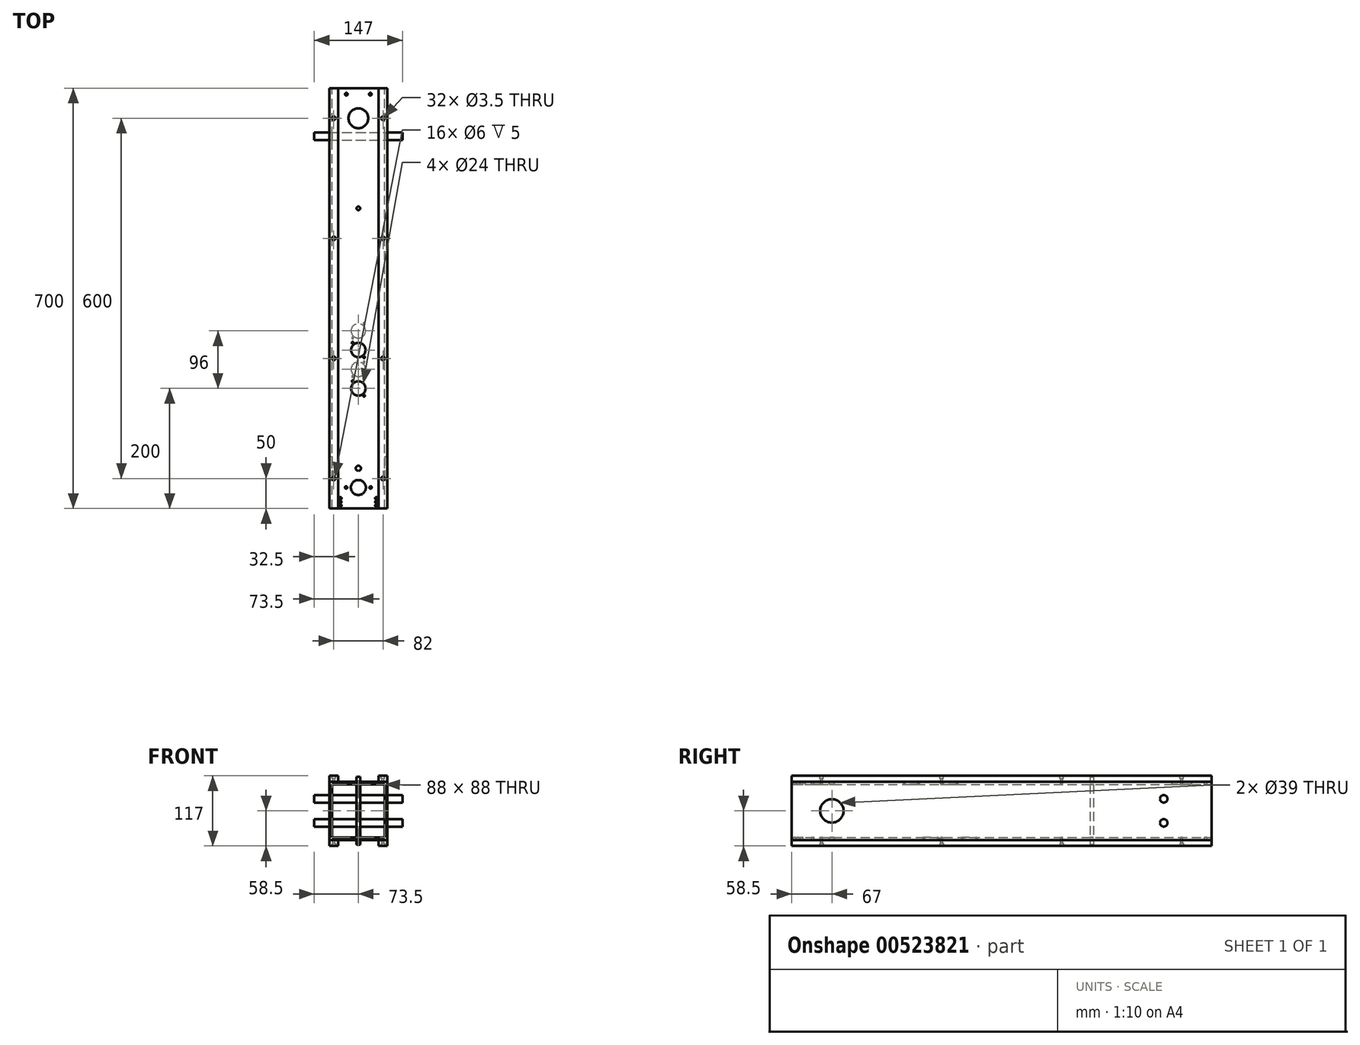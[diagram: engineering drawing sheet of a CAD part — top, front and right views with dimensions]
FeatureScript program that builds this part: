
annotation { "Feature Type Name" : "Feature", "Feature Type Description" : "" }
export const myFeature = defineFeature(function(context is Context, id is Id, definition is map)
    precondition{}
    {
        {
            var Q0;
            Q0=qCreatedBy(makeId("Front.planeOp"),FACE);
            var sketch = newSketch(context, id + "F0", { "sketchPlane" : qUnion([Q0])});
            skLineSegment(sketch, "E0.bottom", {"start": v(0, 0) * mm, "end": v(97, 0) * mm});
            skLineSegment(sketch, "E0.top", {"start": v(0, 97) * mm, "end": v(97, 97) * mm});
            skLineSegment(sketch, "E0.left", {"start": v(0, 0) * mm, "end": v(0, 97) * mm});
            skLineSegment(sketch, "E0.right", {"start": v(97, 0) * mm, "end": v(97, 97) * mm});
            skLineSegment(sketch, "E1.bottom", {"start": v(4.5, 92.5) * mm, "end": v(92.5, 92.5) * mm});
            skLineSegment(sketch, "E1.top", {"start": v(4.5, 4.5) * mm, "end": v(92.5, 4.5) * mm});
            skLineSegment(sketch, "E1.left", {"start": v(4.5, 92.5) * mm, "end": v(4.5, 4.5) * mm});
            skLineSegment(sketch, "E1.right", {"start": v(92.5, 92.5) * mm, "end": v(92.5, 4.5) * mm});
            skSolve(sketch);
        }
        {
            var Q0;
            Q0=makeQuery(id+"F0.imprint","IMPRINT",FACE,{"disambiguationData":[TD([[makeQuery(id+"F0.imprint","IMPRINT",EDGE,{"derivedFrom":sQuery(id+"F0.wireOp",EDGE,"E0.bottom")}),1.0]])]});
            extrude(context, id + "F1", {"entities" : qUnion([Q0]), "depth" : 700 * mm, "offsetDistance" : 25 * mm});
        }
        {
            var Q0;
            Q0=makeQuery(id+"F1.opExtrude","SWEPT_FACE",FACE,{"disambiguationData":[OSD([sQuery(id+"F0.wireOp",EDGE,"E0.top")])]});
            var sketch = newSketch(context, id + "F2", { "sketchPlane" : qUnion([Q0])});
            skLineSegment(sketch, "E2.bottom", {"start": v(0, 0) * mm, "end": v(15, 0) * mm});
            skLineSegment(sketch, "E2.top", {"start": v(0, -700) * mm, "end": v(15, -700) * mm});
            skLineSegment(sketch, "E2.left", {"start": v(0, 0) * mm, "end": v(0, -700) * mm});
            skLineSegment(sketch, "E2.right", {"start": v(15, 0) * mm, "end": v(15, -700) * mm});
            skLineSegment(sketch, "E3.bottom", {"start": v(97, 0) * mm, "end": v(82, 0) * mm});
            skLineSegment(sketch, "E3.top", {"start": v(97, -700) * mm, "end": v(82, -700) * mm});
            skLineSegment(sketch, "E3.left", {"start": v(97, 0) * mm, "end": v(97, -700) * mm});
            skLineSegment(sketch, "E3.right", {"start": v(82, 0) * mm, "end": v(82, -700) * mm});
            skSolve(sketch);
        }
        {
            var Q0;
            Q0 = qSketchRegion(id + "F2", true);
            extrude(context, id + "F3", {"entities" : qUnion([Q0]), "depth" : 10 * mm, "offsetDistance" : 25 * mm});
        }
        {
            var Q0;
            Q0=makeQuery(id+"F1.opExtrude","SWEPT_FACE",FACE,{"disambiguationData":[OSD([sQuery(id+"F0.wireOp",EDGE,"E0.bottom")])]});
            var sketch = newSketch(context, id + "F4", { "sketchPlane" : qUnion([Q0])});
            skLineSegment(sketch, "E4.bottom", {"start": v(0, 700) * mm, "end": v(15, 700) * mm});
            skLineSegment(sketch, "E4.top", {"start": v(0, 0) * mm, "end": v(15, 0) * mm});
            skLineSegment(sketch, "E4.left", {"start": v(0, 700) * mm, "end": v(0, 0) * mm});
            skLineSegment(sketch, "E4.right", {"start": v(15, 700) * mm, "end": v(15, 0) * mm});
            skLineSegment(sketch, "E5.bottom", {"start": v(97, 700) * mm, "end": v(82, 700) * mm});
            skLineSegment(sketch, "E5.top", {"start": v(97, 0) * mm, "end": v(82, 0) * mm});
            skLineSegment(sketch, "E5.left", {"start": v(97, 700) * mm, "end": v(97, 0) * mm});
            skLineSegment(sketch, "E5.right", {"start": v(82, 700) * mm, "end": v(82, 0) * mm});
            skSolve(sketch);
        }
        {
            var Q0;
            Q0 = qSketchRegion(id + "F4", true);
            extrude(context, id + "F5", {"entities" : qUnion([Q0]), "depth" : 10 * mm, "offsetDistance" : 25 * mm});
        }
        {
            var Q0;
            {var subQ0=sQuery(id+"F2.wireOp",EDGE,"E2.right");Q0=makeQuery(id+"F2.imprint","IMPRINT",FACE,{"disambiguationData":[TD([[makeQuery(id+"F2.imprint","IMPRINT",EDGE,{"derivedFrom":subQ0}),1.0]])]});}
            var sketch = newSketch(context, id + "F6", { "sketchPlane" : qUnion([Q0])});
            skLineSegment(sketch, "E6", {"start": v(48.5, -700) * mm, "end": v(48.5, 0) * mm, "construction": true});
            skCircle(sketch, "E7", {"center": v(48.5, -633) * mm, "radius": 4.25 * mm});
            skCircle(sketch, "E8", {"center": v(48.5, -665) * mm, "radius": 12.5 * mm});
            skCircle(sketch, "E9", {"center": v(28, -665) * mm, "radius": 2 * mm});
            skCircle(sketch, "E10", {"center": v(69, -665) * mm, "radius": 2 * mm});
            skLineSegment(sketch, "E11", {"start": v(28, -665) * mm, "end": v(69, -665) * mm, "construction": true});
            skCircle(sketch, "E12", {"center": v(48.5, -500) * mm, "radius": 12 * mm});
            skCircle(sketch, "E13", {"center": v(39, -488) * mm, "radius": 1.5 * mm});
            skCircle(sketch, "E14", {"center": v(58, -512) * mm, "radius": 1.5 * mm});
            skLineSegment(sketch, "E15", {"start": v(58, -512) * mm, "end": v(39, -488) * mm, "construction": true});
            skCircle(sketch, "E16.0.1.0", {"center": v(48.5, -436) * mm, "radius": 12 * mm});
            skCircle(sketch, "E16.0.1.1", {"center": v(39, -424) * mm, "radius": 1.5 * mm});
            skCircle(sketch, "E16.0.1.2", {"center": v(58, -448) * mm, "radius": 1.5 * mm});
            skLineSegment(sketch, "E16.direction1", {"start": v(48.5, -500) * mm, "end": v(74.81, -500) * mm, "construction": true});
            skLineSegment(sketch, "E16.direction2", {"start": v(48.5, -500) * mm, "end": v(48.5, -436) * mm, "construction": true});
            skArc(sketch, "E17", {"start": v(20.5, -683) * mm, "mid": v(18.5, -681) * mm, "end": v(16.5, -683) * mm});
            skArc(sketch, "E18", {"start": v(80.5, -683) * mm, "mid": v(78.5, -681) * mm, "end": v(76.5, -683) * mm});
            skLineSegment(sketch, "E19", {"start": v(48.5, -683) * mm, "end": v(78.5, -683) * mm, "construction": true});
            skLineSegment(sketch, "E20", {"start": v(48.5, -683) * mm, "end": v(18.5, -683) * mm, "construction": true});
            skCircle(sketch, "E21", {"center": v(48.5, -633) * mm, "radius": 19.5 * mm, "construction": true});
            skCircle(sketch, "E22", {"center": v(48.5, -665) * mm, "radius": 8.5 * mm, "construction": true});
            skArc(sketch, "E23", {"start": v(16.5, -695) * mm, "mid": v(18.5, -697) * mm, "end": v(20.5, -695) * mm});
            skArc(sketch, "E24", {"start": v(76.5, -695) * mm, "mid": v(78.5, -697) * mm, "end": v(80.5, -695) * mm});
            skCircle(sketch, "E25", {"center": v(28.5, -10) * mm, "radius": 2.25 * mm});
            skCircle(sketch, "E26", {"center": v(68.5, -10) * mm, "radius": 2.25 * mm});
            skLineSegment(sketch, "E27", {"start": v(28.5, -10) * mm, "end": v(48.5, -10) * mm, "construction": true});
            skLineSegment(sketch, "E28", {"start": v(48.5, -10) * mm, "end": v(68.5, -10) * mm, "construction": true});
            skCircle(sketch, "E29", {"center": v(48.5, -50) * mm, "radius": 16.5 * mm});
            skCircle(sketch, "E30", {"center": v(48.5, -665) * mm, "radius": 6 * mm, "construction": true});
            skCircle(sketch, "E31", {"center": v(48.5, -200) * mm, "radius": 3 * mm});
            skCircle(sketch, "E32", {"center": v(18.5, -683) * mm, "radius": 2 * mm});
            skCircle(sketch, "E33", {"center": v(18.5, -695) * mm, "radius": 2 * mm});
            skLineSegment(sketch, "E34", {"start": v(18.5, -683) * mm, "end": v(18.5, -695) * mm, "construction": true});
            skCircle(sketch, "E35", {"center": v(18.5, -689) * mm, "radius": 2 * mm});
            skCircle(sketch, "E36", {"center": v(78.5, -683) * mm, "radius": 2 * mm});
            skCircle(sketch, "E37", {"center": v(78.5, -695) * mm, "radius": 2 * mm});
            skLineSegment(sketch, "E38", {"start": v(78.5, -683) * mm, "end": v(78.5, -695) * mm, "construction": true});
            skCircle(sketch, "E39", {"center": v(78.5, -689) * mm, "radius": 2 * mm});
            skSolve(sketch);
        }
        {
            var Q0;
            Q0=makeQuery(id+"F6.imprint","IMPRINT",FACE,{"disambiguationData":[TD([[makeQuery(id+"F6.imprint","IMPRINT",EDGE,{"derivedFrom":sQuery(id+"F6.wireOp",EDGE,"E8")}),1.0]])]});
            var Q1;
            Q1=makeQuery(id+"F6.imprint","IMPRINT",FACE,{"disambiguationData":[TD([[makeQuery(id+"F6.imprint","IMPRINT",EDGE,{"derivedFrom":sQuery(id+"F6.wireOp",EDGE,"E12")}),1.0]])]});
            var Q2;
            Q2=makeQuery(id+"F6.imprint","IMPRINT",FACE,{"disambiguationData":[TD([[makeQuery(id+"F6.imprint","IMPRINT",EDGE,{"derivedFrom":sQuery(id+"F6.wireOp",EDGE,"E16.0.1.0")}),1.0]])]});
            var Q3;
            Q3=makeQuery(id+"F6.imprint","IMPRINT",FACE,{"disambiguationData":[TD([[makeQuery(id+"F6.imprint","IMPRINT",EDGE,{"derivedFrom":sQuery(id+"F6.wireOp",EDGE,"E16.0.1.2")}),1.0]])]});
            var Q4;
            Q4=makeQuery(id+"F6.imprint","IMPRINT",FACE,{"disambiguationData":[TD([[makeQuery(id+"F6.imprint","IMPRINT",EDGE,{"derivedFrom":sQuery(id+"F6.wireOp",EDGE,"E16.0.1.1")}),1.0]])]});
            var Q5;
            Q5=makeQuery(id+"F6.imprint","IMPRINT",FACE,{"disambiguationData":[TD([[makeQuery(id+"F6.imprint","IMPRINT",EDGE,{"derivedFrom":sQuery(id+"F6.wireOp",EDGE,"E13")}),1.0]])]});
            var Q6;
            Q6=makeQuery(id+"F6.imprint","IMPRINT",FACE,{"disambiguationData":[TD([[makeQuery(id+"F6.imprint","IMPRINT",EDGE,{"derivedFrom":sQuery(id+"F6.wireOp",EDGE,"E14")}),1.0]])]});
            extrude(context, id + "F7", {"entities" : qUnion([Q0, Q1, Q2, Q3, Q4, Q5, Q6]), "operationType" : NewBodyOperationType.REMOVE, "oppositeDirection" : true, "depth" : 25 * mm, "offsetDistance" : 25 * mm});
        }
        {
            var Q0;
            Q0=makeQuery(id+"F6.imprint","IMPRINT",FACE,{"disambiguationData":[TD([[makeQuery(id+"F6.imprint","IMPRINT",EDGE,{"derivedFrom":sQuery(id+"F6.wireOp",EDGE,"E7")}),1.0]])]});
            var Q1;
            Q1=makeQuery(id+"F6.imprint","IMPRINT",FACE,{"disambiguationData":[TD([[makeQuery(id+"F6.imprint","IMPRINT",EDGE,{"derivedFrom":sQuery(id+"F6.wireOp",EDGE,"E10")}),1.0]])]});
            var Q2;
            Q2=makeQuery(id+"F6.imprint","IMPRINT",FACE,{"disambiguationData":[TD([[makeQuery(id+"F6.imprint","IMPRINT",EDGE,{"derivedFrom":sQuery(id+"F6.wireOp",EDGE,"E9")}),1.0]])]});
            extrude(context, id + "F8", {"entities" : qUnion([Q0, Q1, Q2]), "operationType" : NewBodyOperationType.REMOVE, "oppositeDirection" : true, "depth" : 150 * mm, "offsetDistance" : 25 * mm});
        }
        {
            var Q0;
            Q0=makeQuery(id+"F1.opExtrude","SWEPT_FACE",FACE,{"disambiguationData":[OSD([sQuery(id+"F0.wireOp",EDGE,"E0.bottom")])]});
            var sketch = newSketch(context, id + "F9", { "sketchPlane" : qUnion([Q0])});
            skLineSegment(sketch, "E40", {"start": v(48.5, 700) * mm, "end": v(48.5, 0) * mm, "construction": true});
            skCircle(sketch, "E41", {"center": v(48.5, 468) * mm, "radius": 12 * mm});
            skCircle(sketch, "E42", {"center": v(39, 480) * mm, "radius": 1.5 * mm});
            skCircle(sketch, "E43", {"center": v(58, 456) * mm, "radius": 1.5 * mm});
            skLineSegment(sketch, "E44", {"start": v(58, 456) * mm, "end": v(39, 480) * mm, "construction": true});
            skCircle(sketch, "E45.0.1.0", {"center": v(48.5, 404) * mm, "radius": 12 * mm});
            skCircle(sketch, "E45.0.1.1", {"center": v(58, 392) * mm, "radius": 1.5 * mm});
            skCircle(sketch, "E45.0.1.2", {"center": v(39, 416) * mm, "radius": 1.5 * mm});
            skLineSegment(sketch, "E45.direction1", {"start": v(48.5, 468) * mm, "end": v(75, 468) * mm, "construction": true});
            skLineSegment(sketch, "E45.direction2", {"start": v(48.5, 468) * mm, "end": v(48.5, 404) * mm, "construction": true});
            skSolve(sketch);
        }
        {
            var Q0;
            Q0 = qSketchRegion(id + "F9", true);
            extrude(context, id + "F10", {"entities" : qUnion([Q0]), "operationType" : NewBodyOperationType.REMOVE, "oppositeDirection" : true, "depth" : 25 * mm, "offsetDistance" : 25 * mm});
        }
        {
            var Q0;
            Q0=makeQuery(id+"F1.opExtrude","SWEPT_FACE",FACE,{"disambiguationData":[OSD([sQuery(id+"F0.wireOp",EDGE,"E0.right")])]});
            var sketch = newSketch(context, id + "F11", { "sketchPlane" : qUnion([Q0])});
            skLineSegment(sketch, "E46", {"start": v(-700, 48.5) * mm, "end": v(0, 48.5) * mm, "construction": true});
            skCircle(sketch, "E47", {"center": v(-633, 48.5) * mm, "radius": 19.5 * mm});
            skCircle(sketch, "E48", {"center": v(-80, 68.5) * mm, "radius": 6.26 * mm});
            skCircle(sketch, "E49", {"center": v(-80, 28.5) * mm, "radius": 6.26 * mm});
            skLineSegment(sketch, "E50", {"start": v(-80, 68.5) * mm, "end": v(-80, 48.5) * mm, "construction": true});
            skLineSegment(sketch, "E51", {"start": v(-80, 48.5) * mm, "end": v(-80, 28.5) * mm, "construction": true});
            skSolve(sketch);
        }
        {
            var Q0;
            Q0 = qSketchRegion(id + "F11", true);
            extrude(context, id + "F12", {"entities" : qUnion([Q0]), "operationType" : NewBodyOperationType.REMOVE, "oppositeDirection" : true, "depth" : 150 * mm, "offsetDistance" : 25 * mm});
        }
        {
            var Q0;
            Q0=makeQuery(id+"F6.imprint","IMPRINT",FACE,{"disambiguationData":[TD([[makeQuery(id+"F6.imprint","IMPRINT",EDGE,{"derivedFrom":sQuery(id+"F6.wireOp",EDGE,"E17")}),1.0]])]});
            var Q1;
            Q1=makeQuery(id+"F6.imprint","IMPRINT",FACE,{"disambiguationData":[TD([[makeQuery(id+"F6.imprint","IMPRINT",EDGE,{"derivedFrom":sQuery(id+"F6.wireOp",EDGE,"E18")}),1.0]])]});
            extrude(context, id + "F13", {"entities" : qUnion([Q0, Q1]), "operationType" : NewBodyOperationType.REMOVE, "oppositeDirection" : true, "depth" : 150 * mm, "offsetDistance" : 25 * mm});
        }
        {
            var Q0;
            Q0=makeQuery(id+"F6.imprint","IMPRINT",FACE,{"disambiguationData":[TD([[makeQuery(id+"F6.imprint","IMPRINT",EDGE,{"derivedFrom":sQuery(id+"F6.wireOp",EDGE,"E25")}),1.0]])]});
            var Q1;
            Q1=makeQuery(id+"F6.imprint","IMPRINT",FACE,{"disambiguationData":[TD([[makeQuery(id+"F6.imprint","IMPRINT",EDGE,{"derivedFrom":sQuery(id+"F6.wireOp",EDGE,"E26")}),1.0]])]});
            extrude(context, id + "F14", {"entities" : qUnion([Q0, Q1]), "operationType" : NewBodyOperationType.REMOVE, "oppositeDirection" : true, "depth" : 150 * mm, "offsetDistance" : 25 * mm});
        }
        {
            var Q0;
            Q0=makeQuery(id+"F6.imprint","IMPRINT",FACE,{"disambiguationData":[TD([[makeQuery(id+"F6.imprint","IMPRINT",EDGE,{"derivedFrom":sQuery(id+"F6.wireOp",EDGE,"E29")}),1.0]])]});
            extrude(context, id + "F15", {"entities" : qUnion([Q0]), "operationType" : NewBodyOperationType.REMOVE, "oppositeDirection" : true, "depth" : 50 * mm, "offsetDistance" : 25 * mm});
        }
        {
            var Q0;
            Q0=makeQuery(id+"F11.imprint","IMPRINT",FACE,{"disambiguationData":[TD([[makeQuery(id+"F11.imprint","IMPRINT",EDGE,{"derivedFrom":sQuery(id+"F11.wireOp",EDGE,"E48")}),1.0]])]});
            extrude(context, id + "F16", {"entities" : qUnion([Q0]), "oppositeDirection" : true, "depth" : 122 * mm, "offsetDistance" : 25 * mm, "hasSecondDirection" : true, "secondDirectionOppositeDirection" : false, "secondDirectionDepth" : 25 * mm});
        }
        {
            var Q0;
            Q0=makeQuery(id+"F11.imprint","IMPRINT",FACE,{"disambiguationData":[TD([[makeQuery(id+"F11.imprint","IMPRINT",EDGE,{"derivedFrom":sQuery(id+"F11.wireOp",EDGE,"E49")}),1.0]])]});
            extrude(context, id + "F17", {"entities" : qUnion([Q0]), "oppositeDirection" : true, "depth" : 122 * mm, "offsetDistance" : 25 * mm, "hasSecondDirection" : true, "secondDirectionOppositeDirection" : false, "secondDirectionDepth" : 25 * mm});
        }
        {
            var Q0;
            Q0=makeQuery(id+"F3.opExtrude","CAP_FACE",FACE,{"disambiguationData":[OSD([sQuery(id+"F2.wireOp",EDGE,"E2.bottom"),sQuery(id+"F2.wireOp",EDGE,"E2.top"),sQuery(id+"F2.wireOp",EDGE,"E2.left"),sQuery(id+"F2.wireOp",EDGE,"E2.right")])],"isStart":false});
            var sketch = newSketch(context, id + "F18", { "sketchPlane" : qUnion([Q0])});
            skLineSegment(sketch, "E52", {"start": v(7.5, -700) * mm, "end": v(7.5, 0) * mm, "construction": true});
            skCircle(sketch, "E53", {"center": v(7.5, -50) * mm, "radius": 1.75 * mm});
            skCircle(sketch, "E54", {"center": v(7.5, -50) * mm, "radius": 3 * mm});
            skCircle(sketch, "E55.0.1.0", {"center": v(7.5, -250) * mm, "radius": 3 * mm});
            skCircle(sketch, "E55.0.1.1", {"center": v(7.5, -250) * mm, "radius": 1.75 * mm});
            skCircle(sketch, "E55.0.2.0", {"center": v(7.5, -450) * mm, "radius": 3 * mm});
            skCircle(sketch, "E55.0.2.1", {"center": v(7.5, -450) * mm, "radius": 1.75 * mm});
            skCircle(sketch, "E55.0.3.0", {"center": v(7.5, -650) * mm, "radius": 3 * mm});
            skCircle(sketch, "E55.0.3.1", {"center": v(7.5, -650) * mm, "radius": 1.75 * mm});
            skLineSegment(sketch, "E55.direction1", {"start": v(7.5, -50) * mm, "end": v(89.5, -50) * mm, "construction": true});
            skLineSegment(sketch, "E55.direction2", {"start": v(7.5, -50) * mm, "end": v(7.5, -250) * mm, "construction": true});
            skCircle(sketch, "E56.0.1.0", {"center": v(89.5, -50) * mm, "radius": 3 * mm});
            skCircle(sketch, "E56.2.1.0", {"center": v(89.5, -50) * mm, "radius": 1.75 * mm});
            skCircle(sketch, "E56.0.1.1", {"center": v(89.5, -250) * mm, "radius": 3 * mm});
            skCircle(sketch, "E56.2.1.1", {"center": v(89.5, -250) * mm, "radius": 1.75 * mm});
            skCircle(sketch, "E56.0.1.2", {"center": v(89.5, -450) * mm, "radius": 3 * mm});
            skCircle(sketch, "E56.2.1.2", {"center": v(89.5, -450) * mm, "radius": 1.75 * mm});
            skCircle(sketch, "E56.0.1.3", {"center": v(89.5, -650) * mm, "radius": 3 * mm});
            skCircle(sketch, "E56.2.1.3", {"center": v(89.5, -650) * mm, "radius": 1.75 * mm});
            skSolve(sketch);
        }
        {
            var Q0;
            Q0=makeQuery(id+"F18.imprint","IMPRINT",FACE,{"disambiguationData":[TD([[makeQuery(id+"F18.imprint","IMPRINT",EDGE,{"derivedFrom":sQuery(id+"F18.wireOp",EDGE,"E55.0.3.1")}),1.0]])]});
            var Q1;
            Q1=makeQuery(id+"F18.imprint","IMPRINT",FACE,{"disambiguationData":[TD([[makeQuery(id+"F18.imprint","IMPRINT",EDGE,{"derivedFrom":sQuery(id+"F18.wireOp",EDGE,"E55.0.2.1")}),1.0]])]});
            var Q2;
            Q2=makeQuery(id+"F18.imprint","IMPRINT",FACE,{"disambiguationData":[TD([[makeQuery(id+"F18.imprint","IMPRINT",EDGE,{"derivedFrom":sQuery(id+"F18.wireOp",EDGE,"E55.0.1.1")}),1.0]])]});
            var Q3;
            Q3=makeQuery(id+"F18.imprint","IMPRINT",FACE,{"disambiguationData":[TD([[makeQuery(id+"F18.imprint","IMPRINT",EDGE,{"derivedFrom":sQuery(id+"F18.wireOp",EDGE,"E53")}),1.0]])]});
            var Q4;
            Q4=makeQuery(id+"F18.imprint","IMPRINT",FACE,{"disambiguationData":[TD([[makeQuery(id+"F18.imprint","IMPRINT",EDGE,{"derivedFrom":sQuery(id+"F18.wireOp",EDGE,"E56.2.1.0")}),1.0]])]});
            var Q5;
            Q5=makeQuery(id+"F18.imprint","IMPRINT",FACE,{"disambiguationData":[TD([[makeQuery(id+"F18.imprint","IMPRINT",EDGE,{"derivedFrom":sQuery(id+"F18.wireOp",EDGE,"E56.2.1.1")}),1.0]])]});
            var Q6;
            Q6=makeQuery(id+"F18.imprint","IMPRINT",FACE,{"disambiguationData":[TD([[makeQuery(id+"F18.imprint","IMPRINT",EDGE,{"derivedFrom":sQuery(id+"F18.wireOp",EDGE,"E56.2.1.2")}),1.0]])]});
            var Q7;
            Q7=makeQuery(id+"F18.imprint","IMPRINT",FACE,{"disambiguationData":[TD([[makeQuery(id+"F18.imprint","IMPRINT",EDGE,{"derivedFrom":sQuery(id+"F18.wireOp",EDGE,"E56.2.1.3")}),1.0]])]});
            extrude(context, id + "F19", {"entities" : qUnion([Q0, Q1, Q2, Q3, Q4, Q5, Q6, Q7]), "operationType" : NewBodyOperationType.REMOVE, "oppositeDirection" : true, "depth" : 150 * mm, "offsetDistance" : 25 * mm});
        }
        {
            var Q0;
            Q0=makeQuery(id+"F18.imprint","IMPRINT",FACE,{"disambiguationData":[TD([[makeQuery(id+"F18.imprint","IMPRINT",EDGE,{"derivedFrom":sQuery(id+"F18.wireOp",EDGE,"E55.0.3.0")}),1.0]])]});
            var Q1;
            Q1=makeQuery(id+"F18.imprint","IMPRINT",FACE,{"disambiguationData":[TD([[makeQuery(id+"F18.imprint","IMPRINT",EDGE,{"derivedFrom":sQuery(id+"F18.wireOp",EDGE,"E56.0.1.3")}),1.0]])]});
            var Q2;
            Q2=makeQuery(id+"F18.imprint","IMPRINT",FACE,{"disambiguationData":[TD([[makeQuery(id+"F18.imprint","IMPRINT",EDGE,{"derivedFrom":sQuery(id+"F18.wireOp",EDGE,"E55.0.2.0")}),1.0]])]});
            var Q3;
            Q3=makeQuery(id+"F18.imprint","IMPRINT",FACE,{"disambiguationData":[TD([[makeQuery(id+"F18.imprint","IMPRINT",EDGE,{"derivedFrom":sQuery(id+"F18.wireOp",EDGE,"E56.0.1.2")}),1.0]])]});
            var Q4;
            Q4=makeQuery(id+"F18.imprint","IMPRINT",FACE,{"disambiguationData":[TD([[makeQuery(id+"F18.imprint","IMPRINT",EDGE,{"derivedFrom":sQuery(id+"F18.wireOp",EDGE,"E55.0.1.0")}),1.0]])]});
            var Q5;
            Q5=makeQuery(id+"F18.imprint","IMPRINT",FACE,{"disambiguationData":[TD([[makeQuery(id+"F18.imprint","IMPRINT",EDGE,{"derivedFrom":sQuery(id+"F18.wireOp",EDGE,"E56.0.1.1")}),1.0]])]});
            var Q6;
            Q6=makeQuery(id+"F18.imprint","IMPRINT",FACE,{"disambiguationData":[TD([[makeQuery(id+"F18.imprint","IMPRINT",EDGE,{"derivedFrom":sQuery(id+"F18.wireOp",EDGE,"E53")}),-1.0]])]});
            var Q7;
            Q7=makeQuery(id+"F18.imprint","IMPRINT",FACE,{"disambiguationData":[TD([[makeQuery(id+"F18.imprint","IMPRINT",EDGE,{"derivedFrom":sQuery(id+"F18.wireOp",EDGE,"E56.0.1.0")}),1.0]])]});
            extrude(context, id + "F20", {"entities" : qUnion([Q0, Q1, Q2, Q3, Q4, Q5, Q6, Q7]), "operationType" : NewBodyOperationType.REMOVE, "oppositeDirection" : true, "depth" : 5 * mm, "offsetDistance" : 25 * mm});
        }
        {
            var Q0;
            Q0=makeQuery(id+"F5.opExtrude","CAP_FACE",FACE,{"disambiguationData":[OSD([sQuery(id+"F4.wireOp",EDGE,"E5.bottom"),sQuery(id+"F4.wireOp",EDGE,"E5.top"),sQuery(id+"F4.wireOp",EDGE,"E5.left"),sQuery(id+"F4.wireOp",EDGE,"E5.right")])],"isStart":false});
            var sketch = newSketch(context, id + "F21", { "sketchPlane" : qUnion([Q0])});
            skCircle(sketch, "E57", {"center": v(89.5, 50) * mm, "radius": 3 * mm});
            skCircle(sketch, "E58.0.1.0", {"center": v(89.5, 250) * mm, "radius": 3 * mm});
            skCircle(sketch, "E58.0.2.0", {"center": v(89.5, 450) * mm, "radius": 3 * mm});
            skCircle(sketch, "E58.0.3.0", {"center": v(89.5, 650) * mm, "radius": 3 * mm});
            skCircle(sketch, "E58.1.0.0", {"center": v(7.5, 50) * mm, "radius": 3 * mm});
            skCircle(sketch, "E58.1.1.0", {"center": v(7.5, 250) * mm, "radius": 3 * mm});
            skCircle(sketch, "E58.1.2.0", {"center": v(7.5, 450) * mm, "radius": 3 * mm});
            skCircle(sketch, "E58.1.3.0", {"center": v(7.5, 650) * mm, "radius": 3 * mm});
            skLineSegment(sketch, "E58.direction1", {"start": v(89.5, 50) * mm, "end": v(7.5, 50) * mm, "construction": true});
            skLineSegment(sketch, "E58.direction2", {"start": v(89.5, 50) * mm, "end": v(89.5, 250) * mm, "construction": true});
            skSolve(sketch);
        }
        {
            var Q0;
            Q0=makeQuery(id+"F21.imprint","IMPRINT",FACE,{"disambiguationData":[TD([[makeQuery(id+"F21.imprint","IMPRINT",EDGE,{"derivedFrom":sQuery(id+"F21.wireOp",EDGE,"E57")}),1.0]])]});
            var Q1;
            Q1=makeQuery(id+"F21.imprint","IMPRINT",FACE,{"disambiguationData":[TD([[makeQuery(id+"F21.imprint","IMPRINT",EDGE,{"derivedFrom":sQuery(id+"F21.wireOp",EDGE,"E58.1.0.0")}),1.0]])]});
            var Q2;
            Q2=makeQuery(id+"F21.imprint","IMPRINT",FACE,{"disambiguationData":[TD([[makeQuery(id+"F21.imprint","IMPRINT",EDGE,{"derivedFrom":sQuery(id+"F21.wireOp",EDGE,"E58.0.1.0")}),1.0]])]});
            var Q3;
            Q3=makeQuery(id+"F21.imprint","IMPRINT",FACE,{"disambiguationData":[TD([[makeQuery(id+"F21.imprint","IMPRINT",EDGE,{"derivedFrom":sQuery(id+"F21.wireOp",EDGE,"E58.1.1.0")}),1.0]])]});
            var Q4;
            Q4=makeQuery(id+"F21.imprint","IMPRINT",FACE,{"disambiguationData":[TD([[makeQuery(id+"F21.imprint","IMPRINT",EDGE,{"derivedFrom":sQuery(id+"F21.wireOp",EDGE,"E58.1.2.0")}),1.0]])]});
            var Q5;
            Q5=makeQuery(id+"F21.imprint","IMPRINT",FACE,{"disambiguationData":[TD([[makeQuery(id+"F21.imprint","IMPRINT",EDGE,{"derivedFrom":sQuery(id+"F21.wireOp",EDGE,"E58.0.2.0")}),1.0]])]});
            var Q6;
            Q6=makeQuery(id+"F21.imprint","IMPRINT",FACE,{"disambiguationData":[TD([[makeQuery(id+"F21.imprint","IMPRINT",EDGE,{"derivedFrom":sQuery(id+"F21.wireOp",EDGE,"E58.1.3.0")}),1.0]])]});
            var Q7;
            Q7=makeQuery(id+"F21.imprint","IMPRINT",FACE,{"disambiguationData":[TD([[makeQuery(id+"F21.imprint","IMPRINT",EDGE,{"derivedFrom":sQuery(id+"F21.wireOp",EDGE,"E58.0.3.0")}),1.0]])]});
            extrude(context, id + "F22", {"entities" : qUnion([Q0, Q1, Q2, Q3, Q4, Q5, Q6, Q7]), "operationType" : NewBodyOperationType.REMOVE, "oppositeDirection" : true, "depth" : 5 * mm, "offsetDistance" : 25 * mm});
        }
        {
            var Q0;
            Q0=makeQuery(id+"F6.imprint","IMPRINT",FACE,{"disambiguationData":[TD([[makeQuery(id+"F6.imprint","IMPRINT",EDGE,{"derivedFrom":sQuery(id+"F6.wireOp",EDGE,"E31")}),1.0]])]});
            extrude(context, id + "F23", {"entities" : qUnion([Q0]), "operationType" : NewBodyOperationType.REMOVE, "oppositeDirection" : true, "depth" : 120 * mm, "offsetDistance" : 25 * mm});
        }
        {
            var Q0;
            Q0=makeQuery(id+"F6.imprint","IMPRINT",FACE,{"disambiguationData":[TD([[makeQuery(id+"F6.imprint","IMPRINT",EDGE,{"derivedFrom":sQuery(id+"F6.wireOp",EDGE,"E31")}),1.0]])]});
            extrude(context, id + "F24", {"entities" : qUnion([Q0]), "operationType" : NewBodyOperationType.ADD, "depth" : 8 * mm, "offsetDistance" : 25 * mm, "hasSecondDirection" : true, "secondDirectionOppositeDirection" : true, "secondDirectionDepth" : 105 * mm});
        }
        {
            var Q0;
            {var subQ0=sQuery(id+"F6.wireOp",EDGE,"E32");var subQ1=makeQuery(id+"F6.imprint","IMPRINT",VERTEX,{"disambiguationData":[OD(0.0)],"derivedFrom":subQ0});Q0=makeQuery(id+"F6.imprint","IMPRINT",FACE,{"disambiguationData":[TD([[makeQuery(id+"F6.imprint","IMPRINT",EDGE,{"disambiguationData":[TD([[subQ1,1.0]])],"derivedFrom":subQ0}),1.0]])]});}
            var Q1;
            Q1=makeQuery(id+"F6.imprint","IMPRINT",FACE,{"disambiguationData":[TD([[makeQuery(id+"F6.imprint","IMPRINT",EDGE,{"derivedFrom":sQuery(id+"F6.wireOp",EDGE,"E35")}),1.0]])]});
            var Q2;
            {var subQ0=sQuery(id+"F6.wireOp",EDGE,"E33");var subQ1=makeQuery(id+"F6.imprint","IMPRINT",VERTEX,{"disambiguationData":[OD(0.0)],"derivedFrom":subQ0});Q2=makeQuery(id+"F6.imprint","IMPRINT",FACE,{"disambiguationData":[TD([[makeQuery(id+"F6.imprint","IMPRINT",EDGE,{"disambiguationData":[TD([[subQ1,1.0]])],"derivedFrom":subQ0}),1.0]])]});}
            var Q3;
            {var subQ0=sQuery(id+"F6.wireOp",EDGE,"E36");var subQ1=makeQuery(id+"F6.imprint","IMPRINT",VERTEX,{"disambiguationData":[OD(0.0)],"derivedFrom":subQ0});Q3=makeQuery(id+"F6.imprint","IMPRINT",FACE,{"disambiguationData":[TD([[makeQuery(id+"F6.imprint","IMPRINT",EDGE,{"disambiguationData":[TD([[subQ1,1.0]])],"derivedFrom":subQ0}),1.0]])]});}
            var Q4;
            Q4=makeQuery(id+"F6.imprint","IMPRINT",FACE,{"disambiguationData":[TD([[makeQuery(id+"F6.imprint","IMPRINT",EDGE,{"derivedFrom":sQuery(id+"F6.wireOp",EDGE,"E39")}),1.0]])]});
            var Q5;
            {var subQ0=sQuery(id+"F6.wireOp",EDGE,"E37");var subQ1=makeQuery(id+"F6.imprint","IMPRINT",VERTEX,{"disambiguationData":[OD(0.0)],"derivedFrom":subQ0});Q5=makeQuery(id+"F6.imprint","IMPRINT",FACE,{"disambiguationData":[TD([[makeQuery(id+"F6.imprint","IMPRINT",EDGE,{"disambiguationData":[TD([[subQ1,1.0]])],"derivedFrom":subQ0}),1.0]])]});}
            extrude(context, id + "F25", {"entities" : qUnion([Q0, Q1, Q2, Q3, Q4, Q5]), "operationType" : NewBodyOperationType.REMOVE, "oppositeDirection" : true, "depth" : 150 * mm, "offsetDistance" : 25 * mm});
        }
    });
